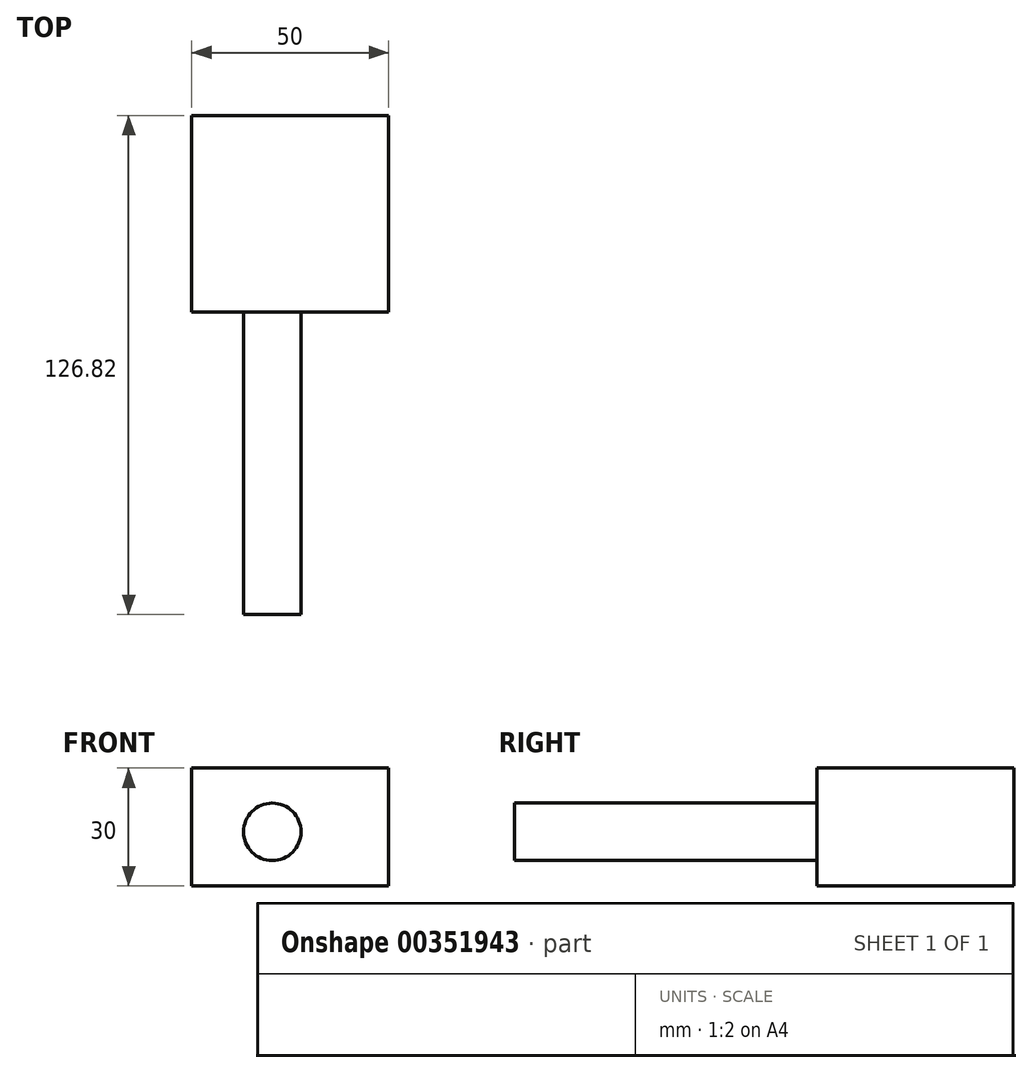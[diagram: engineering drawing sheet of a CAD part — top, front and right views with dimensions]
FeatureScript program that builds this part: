
annotation { "Feature Type Name" : "Feature", "Feature Type Description" : "" }
export const myFeature = defineFeature(function(context is Context, id is Id, definition is map)
    precondition{}
    {
        {
            var Q0;
            Q0=qCreatedBy(makeId("Right.planeOp"),FACE);
            var sketch = newSketch(context, id + "F0", { "sketchPlane" : qUnion([Q0])});
            skSolve(sketch);
        }
        {
            var Q0;
            Q0=qCreatedBy(makeId("Right.planeOp"),FACE);
            var sketch = newSketch(context, id + "F1", { "sketchPlane" : qUnion([Q0])});
            skLineSegment(sketch, "E0.bottom", {"start": v(0, 0) * mm, "end": v(50, 0) * mm});
            skLineSegment(sketch, "E0.top", {"start": v(0, 30) * mm, "end": v(50, 30) * mm});
            skLineSegment(sketch, "E0.left", {"start": v(0, 0) * mm, "end": v(0, 30) * mm});
            skLineSegment(sketch, "E0.right", {"start": v(50, 0) * mm, "end": v(50, 30) * mm});
            skSolve(sketch);
        }
        {
            var Q0;
            Q0 = qSketchRegion(id + "F0", true);
            var Q1;
            Q1=makeQuery(id+"F1.imprint","IMPRINT",FACE,{"disambiguationData":[TD([[makeQuery(id+"F1.imprint","IMPRINT",EDGE,{"derivedFrom":sQuery(id+"F1.wireOp",EDGE,"E0.bottom")}),1.0]])]});
            extrude(context, id + "F2", {"entities" : qUnion([Q0, Q1]), "depth" : 50 * mm});
        }
        {
            var Q0;
            Q0=makeQuery(id+"F2.opExtrude","SWEPT_FACE",FACE,{"disambiguationData":[OSD([sQuery(id+"F1.wireOp",EDGE,"E0.left")])]});
            var sketch = newSketch(context, id + "F3", { "sketchPlane" : qUnion([Q0])});
            skCircle(sketch, "E1", {"center": v(8.74, 22.29) * mm, "radius": 3.09 * mm});
            skCircle(sketch, "E2", {"center": v(32.4, 22.29) * mm, "radius": 2.77 * mm});
            skCircle(sketch, "E3", {"center": v(20.45, 13.79) * mm, "radius": 7.3 * mm});
            skSolve(sketch);
        }
        {
            var Q0;
            Q0=makeQuery(id+"F3.imprint","IMPRINT",FACE,{"disambiguationData":[TD([[makeQuery(id+"F3.imprint","IMPRINT",EDGE,{"derivedFrom":sQuery(id+"F3.wireOp",EDGE,"E3")}),1.0]])]});
            extrude(context, id + "F4", {"entities" : qUnion([Q0]), "operationType" : NewBodyOperationType.ADD, "endBound" : BoundingType.THROUGH_ALL, "depth" : 25 * mm});
        }
        {
            var Q0;
            Q0=makeQuery(id+"F4.opExtrude","CAP_FACE",FACE,{"disambiguationData":[OSD([sQuery(id+"F3.wireOp",EDGE,"E3")])],"isStart":false});
            extrude(context, id + "F5", {"entities" : qUnion([Q0]), "operationType" : NewBodyOperationType.ADD, "oppositeDirection" : true, "depth" : 116.5 * mm});
        }
    });
